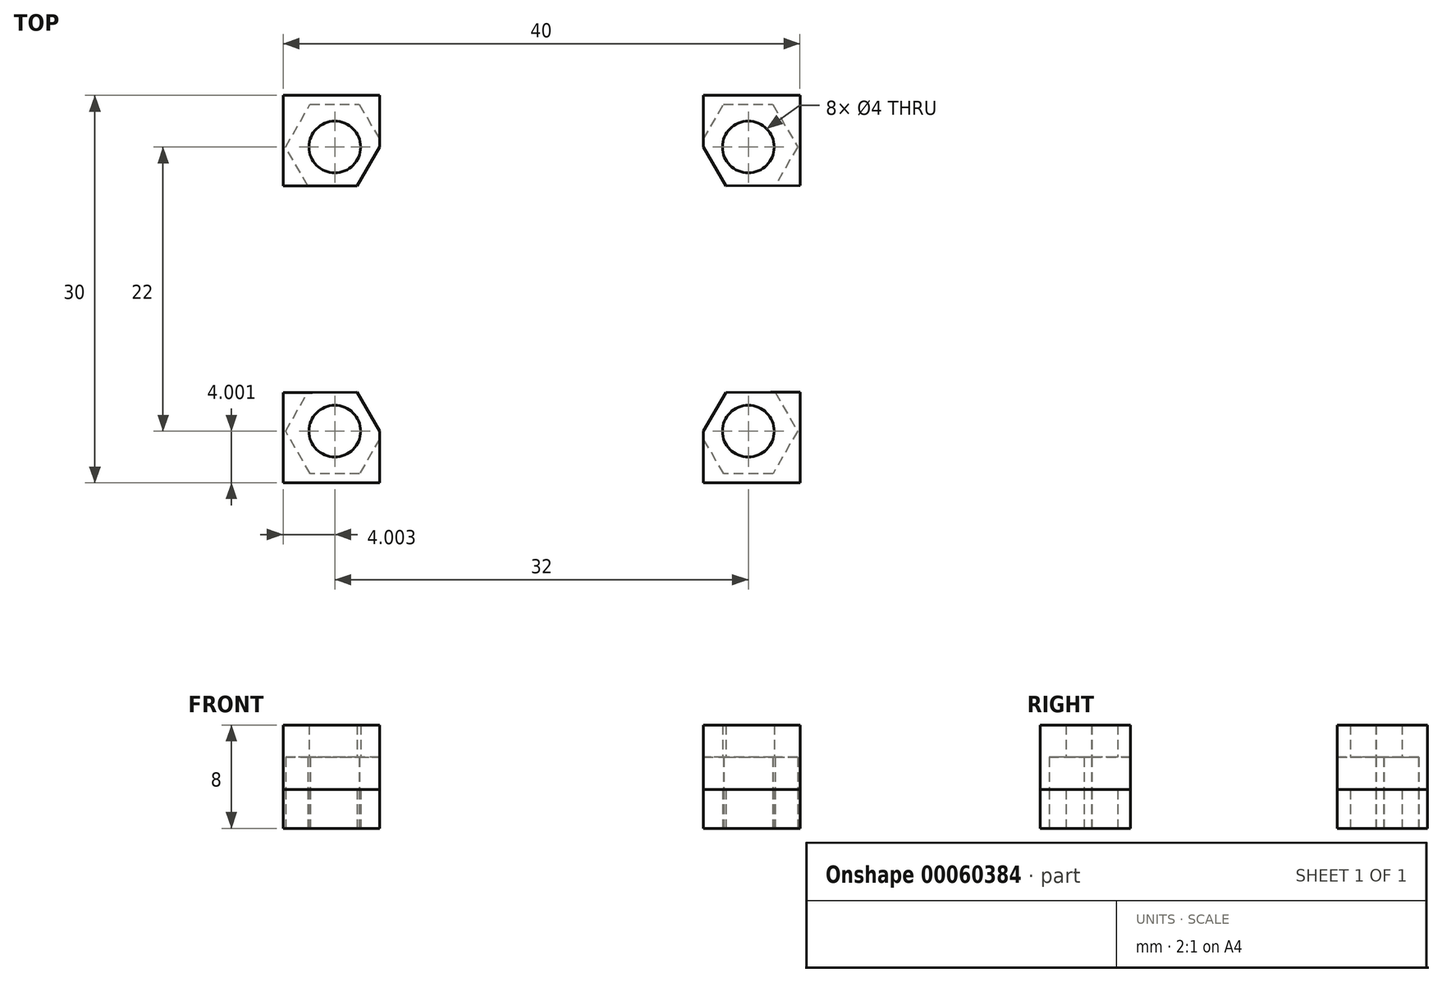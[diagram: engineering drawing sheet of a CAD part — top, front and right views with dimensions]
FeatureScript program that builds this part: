
annotation { "Feature Type Name" : "Feature", "Feature Type Description" : "" }
export const myFeature = defineFeature(function(context is Context, id is Id, definition is map)
    precondition{}
    {
        {
            var Q0;
            Q0=qCreatedBy(makeId("Top.planeOp"),FACE);
            var sketch = newSketch(context, id + "F0", { "sketchPlane" : qUnion([Q0])});
            skCircle(sketch, "E0.cCircle", {"center": v(0, 0) * mm, "radius": 3 * mm, "construction": true});
            skLineSegment(sketch, "E0.0", {"start": v(1.73, 3) * mm, "end": v(3.46, 0) * mm});
            skLineSegment(sketch, "E0.1", {"start": v(3.46, 0) * mm, "end": v(1.74, -3) * mm});
            skLineSegment(sketch, "E0.2", {"start": v(1.74, -3) * mm, "end": v(-1.73, -3) * mm});
            skLineSegment(sketch, "E0.3", {"start": v(-1.73, -3) * mm, "end": v(-3.46, 0) * mm});
            skLineSegment(sketch, "E0.4", {"start": v(-3.46, 0) * mm, "end": v(-1.74, 3) * mm});
            skLineSegment(sketch, "E0.5", {"start": v(-1.74, 3) * mm, "end": v(1.73, 3) * mm});
            skPoint(sketch, "E0.0.midPoint", {"position": v(2.6, 1.5) * mm});
            skCircle(sketch, "E1", {"center": v(0, 0) * mm, "radius": 1.5 * mm});
            skLineSegment(sketch, "E2.bottom", {"start": v(16.24, 59.41) * mm, "end": v(56.24, 59.41) * mm});
            skLineSegment(sketch, "E2.top", {"start": v(16.24, 29.41) * mm, "end": v(56.24, 29.41) * mm});
            skLineSegment(sketch, "E2.left", {"start": v(16.24, 59.41) * mm, "end": v(16.24, 29.41) * mm});
            skLineSegment(sketch, "E2.right", {"start": v(56.24, 59.41) * mm, "end": v(56.24, 29.41) * mm});
            skPoint(sketch, "E3.0.midPoint", {"position": v(22.84, 56.92) * mm});
            skLineSegment(sketch, "E3.3", {"start": v(18.52, 52.4) * mm, "end": v(16.78, 55.4) * mm, "construction": true});
            skLineSegment(sketch, "E3.2", {"start": v(21.98, 52.41) * mm, "end": v(18.52, 52.4) * mm});
            skLineSegment(sketch, "E3.1", {"start": v(23.7, 55.42) * mm, "end": v(21.98, 52.41) * mm});
            skLineSegment(sketch, "E3.0", {"start": v(21.97, 58.41) * mm, "end": v(23.7, 55.42) * mm, "construction": true});
            skLineSegment(sketch, "E3.4", {"start": v(16.78, 55.4) * mm, "end": v(18.5, 58.4) * mm, "construction": true});
            skLineSegment(sketch, "E3.5", {"start": v(18.5, 58.4) * mm, "end": v(21.97, 58.41) * mm, "construction": true});
            skCircle(sketch, "E4", {"center": v(20.24, 55.41) * mm, "radius": 1.5 * mm, "construction": true});
            skCircle(sketch, "E3.cCircle", {"center": v(20.24, 55.41) * mm, "radius": 3 * mm, "construction": true});
            skPoint(sketch, "E5.0.midPoint", {"position": v(22.84, 34.92) * mm});
            skLineSegment(sketch, "E5.3", {"start": v(18.52, 30.4) * mm, "end": v(16.78, 33.4) * mm, "construction": true});
            skLineSegment(sketch, "E5.2", {"start": v(21.98, 30.41) * mm, "end": v(18.52, 30.4) * mm, "construction": true});
            skLineSegment(sketch, "E5.1", {"start": v(23.7, 33.42) * mm, "end": v(21.98, 30.41) * mm, "construction": true});
            skLineSegment(sketch, "E5.0", {"start": v(21.97, 36.41) * mm, "end": v(23.7, 33.42) * mm});
            skLineSegment(sketch, "E5.4", {"start": v(16.78, 33.4) * mm, "end": v(18.5, 36.4) * mm, "construction": true});
            skLineSegment(sketch, "E5.5", {"start": v(18.5, 36.4) * mm, "end": v(21.97, 36.41) * mm});
            skCircle(sketch, "E6", {"center": v(20.24, 33.41) * mm, "radius": 1.5 * mm, "construction": true});
            skCircle(sketch, "E5.cCircle", {"center": v(20.24, 33.41) * mm, "radius": 3 * mm, "construction": true});
            skPoint(sketch, "E7.0.midPoint", {"position": v(54.84, 56.92) * mm});
            skLineSegment(sketch, "E7.3", {"start": v(50.52, 52.4) * mm, "end": v(48.78, 55.4) * mm});
            skLineSegment(sketch, "E7.2", {"start": v(53.98, 52.41) * mm, "end": v(50.52, 52.4) * mm});
            skLineSegment(sketch, "E7.1", {"start": v(55.7, 55.42) * mm, "end": v(53.98, 52.41) * mm, "construction": true});
            skLineSegment(sketch, "E7.0", {"start": v(53.97, 58.41) * mm, "end": v(55.7, 55.42) * mm, "construction": true});
            skLineSegment(sketch, "E7.4", {"start": v(48.78, 55.4) * mm, "end": v(50.5, 58.4) * mm, "construction": true});
            skLineSegment(sketch, "E7.5", {"start": v(50.5, 58.4) * mm, "end": v(53.97, 58.41) * mm, "construction": true});
            skCircle(sketch, "E8", {"center": v(52.24, 55.41) * mm, "radius": 1.5 * mm, "construction": true});
            skCircle(sketch, "E7.cCircle", {"center": v(52.24, 55.41) * mm, "radius": 3 * mm, "construction": true});
            skPoint(sketch, "E9.0.midPoint", {"position": v(54.84, 34.92) * mm});
            skLineSegment(sketch, "E9.3", {"start": v(50.52, 30.4) * mm, "end": v(48.78, 33.4) * mm, "construction": true});
            skLineSegment(sketch, "E9.2", {"start": v(53.98, 30.41) * mm, "end": v(50.52, 30.4) * mm, "construction": true});
            skLineSegment(sketch, "E9.1", {"start": v(55.7, 33.42) * mm, "end": v(53.98, 30.41) * mm, "construction": true});
            skLineSegment(sketch, "E9.0", {"start": v(53.97, 36.41) * mm, "end": v(55.7, 33.42) * mm, "construction": true});
            skLineSegment(sketch, "E9.4", {"start": v(48.78, 33.4) * mm, "end": v(50.5, 36.4) * mm});
            skLineSegment(sketch, "E9.5", {"start": v(50.5, 36.4) * mm, "end": v(53.97, 36.41) * mm});
            skCircle(sketch, "E10", {"center": v(52.24, 33.41) * mm, "radius": 1.5 * mm, "construction": true});
            skCircle(sketch, "E9.cCircle", {"center": v(52.24, 33.41) * mm, "radius": 3 * mm, "construction": true});
            skLineSegment(sketch, "E11", {"start": v(48.78, 33.4) * mm, "end": v(48.78, 29.41) * mm});
            skLineSegment(sketch, "E12", {"start": v(53.97, 36.41) * mm, "end": v(56.24, 36.41) * mm});
            skCircle(sketch, "E13.0", {"center": v(52.24, 33.41) * mm, "radius": 2 * mm});
            skLineSegment(sketch, "E14.0", {"start": v(50.34, 30.1) * mm, "end": v(48.52, 33.25) * mm});
            skLineSegment(sketch, "E14.1", {"start": v(54.15, 30.11) * mm, "end": v(50.34, 30.1) * mm});
            skLineSegment(sketch, "E14.2", {"start": v(56.05, 33.42) * mm, "end": v(54.15, 30.11) * mm});
            skLineSegment(sketch, "E14.3", {"start": v(54.23, 36.56) * mm, "end": v(56.05, 33.42) * mm});
            skLineSegment(sketch, "E15", {"start": v(23.7, 33.42) * mm, "end": v(23.7, 29.41) * mm});
            skLineSegment(sketch, "E16", {"start": v(18.5, 36.4) * mm, "end": v(16.24, 36.4) * mm});
            skLineSegment(sketch, "E17", {"start": v(18.52, 52.4) * mm, "end": v(16.24, 52.4) * mm});
            skLineSegment(sketch, "E18", {"start": v(23.7, 55.42) * mm, "end": v(23.7, 59.41) * mm});
            skLineSegment(sketch, "E19", {"start": v(53.98, 52.41) * mm, "end": v(56.24, 52.42) * mm});
            skLineSegment(sketch, "E20", {"start": v(48.78, 55.4) * mm, "end": v(48.78, 59.41) * mm});
            skCircle(sketch, "E21.0", {"center": v(52.24, 55.41) * mm, "radius": 2 * mm});
            skCircle(sketch, "E22.0", {"center": v(20.24, 55.41) * mm, "radius": 2 * mm});
            skCircle(sketch, "E23.0", {"center": v(20.24, 33.41) * mm, "radius": 2 * mm});
            skLineSegment(sketch, "E24.0", {"start": v(22.14, 58.71) * mm, "end": v(23.97, 55.57) * mm});
            skLineSegment(sketch, "E24.1", {"start": v(18.33, 58.7) * mm, "end": v(22.14, 58.71) * mm});
            skLineSegment(sketch, "E24.2", {"start": v(16.43, 55.4) * mm, "end": v(18.33, 58.7) * mm});
            skLineSegment(sketch, "E24.3", {"start": v(18.26, 52.26) * mm, "end": v(16.43, 55.4) * mm});
            skLineSegment(sketch, "E25.0", {"start": v(16.43, 33.4) * mm, "end": v(18.24, 36.56) * mm});
            skLineSegment(sketch, "E25.1", {"start": v(18.34, 30.1) * mm, "end": v(16.43, 33.4) * mm});
            skLineSegment(sketch, "E25.2", {"start": v(22.15, 30.11) * mm, "end": v(18.34, 30.1) * mm});
            skLineSegment(sketch, "E25.3", {"start": v(23.97, 33.27) * mm, "end": v(22.15, 30.11) * mm});
            skLineSegment(sketch, "E26.0", {"start": v(56.05, 55.42) * mm, "end": v(54.24, 52.26) * mm});
            skLineSegment(sketch, "E26.1", {"start": v(54.14, 58.71) * mm, "end": v(56.05, 55.42) * mm});
            skLineSegment(sketch, "E26.2", {"start": v(50.33, 58.7) * mm, "end": v(54.14, 58.71) * mm});
            skLineSegment(sketch, "E26.3", {"start": v(48.52, 55.55) * mm, "end": v(50.33, 58.7) * mm});
            skSolve(sketch);
        }
        {
            var Q0;
            {var subQ12=sQuery(id+"F0.wireOp",EDGE,"E14.1");Q0=makeQuery(id+"F0.imprint","IMPRINT",FACE,{"disambiguationData":[TD([[makeQuery(id+"F0.imprint","IMPRINT",EDGE,{"derivedFrom":subQ12}),1.0]])]});}
            var Q1;
            {var subQ6=sQuery(id+"F0.wireOp",EDGE,"E9.4");Q1=makeQuery(id+"F0.imprint","IMPRINT",FACE,{"disambiguationData":[TD([[makeQuery(id+"F0.imprint","IMPRINT",EDGE,{"derivedFrom":subQ6}),-1.0]])]});}
            var Q2;
            {var subQ5=sQuery(id+"F0.wireOp",EDGE,"E25.1");Q2=makeQuery(id+"F0.imprint","IMPRINT",FACE,{"disambiguationData":[TD([[makeQuery(id+"F0.imprint","IMPRINT",EDGE,{"derivedFrom":subQ5}),1.0]])]});}
            var Q3;
            {var subQ5=sQuery(id+"F0.wireOp",EDGE,"E5.0");Q3=makeQuery(id+"F0.imprint","IMPRINT",FACE,{"disambiguationData":[TD([[makeQuery(id+"F0.imprint","IMPRINT",EDGE,{"derivedFrom":subQ5}),-1.0]])]});}
            var Q4;
            {var subQ11=sQuery(id+"F0.wireOp",EDGE,"E24.1");Q4=makeQuery(id+"F0.imprint","IMPRINT",FACE,{"disambiguationData":[TD([[makeQuery(id+"F0.imprint","IMPRINT",EDGE,{"derivedFrom":subQ11}),1.0]])]});}
            var Q5;
            {var subQ5=sQuery(id+"F0.wireOp",EDGE,"E3.2");Q5=makeQuery(id+"F0.imprint","IMPRINT",FACE,{"disambiguationData":[TD([[makeQuery(id+"F0.imprint","IMPRINT",EDGE,{"derivedFrom":subQ5}),-1.0]])]});}
            var Q6;
            {var subQ7=sQuery(id+"F0.wireOp",EDGE,"E26.1");Q6=makeQuery(id+"F0.imprint","IMPRINT",FACE,{"disambiguationData":[TD([[makeQuery(id+"F0.imprint","IMPRINT",EDGE,{"derivedFrom":subQ7}),1.0]])]});}
            var Q7;
            {var subQ1=sQuery(id+"F0.wireOp",EDGE,"E7.3");Q7=makeQuery(id+"F0.imprint","IMPRINT",FACE,{"disambiguationData":[TD([[makeQuery(id+"F0.imprint","IMPRINT",EDGE,{"derivedFrom":subQ1}),-1.0]])]});}
            extrude(context, id + "F1", {"entities" : qUnion([Q0, Q1, Q2, Q3, Q4, Q5, Q6, Q7]), "depth" : 3 * mm});
        }
        {
            var Q0;
            {var subQ12=sQuery(id+"F0.wireOp",EDGE,"E14.1");Q0=makeQuery(id+"F0.imprint","IMPRINT",FACE,{"disambiguationData":[TD([[makeQuery(id+"F0.imprint","IMPRINT",EDGE,{"derivedFrom":subQ12}),1.0]])]});}
            var Q1;
            {var subQ7=sQuery(id+"F0.wireOp",EDGE,"E26.1");Q1=makeQuery(id+"F0.imprint","IMPRINT",FACE,{"disambiguationData":[TD([[makeQuery(id+"F0.imprint","IMPRINT",EDGE,{"derivedFrom":subQ7}),1.0]])]});}
            var Q2;
            {var subQ11=sQuery(id+"F0.wireOp",EDGE,"E24.1");Q2=makeQuery(id+"F0.imprint","IMPRINT",FACE,{"disambiguationData":[TD([[makeQuery(id+"F0.imprint","IMPRINT",EDGE,{"derivedFrom":subQ11}),1.0]])]});}
            var Q3;
            {var subQ5=sQuery(id+"F0.wireOp",EDGE,"E25.1");Q3=makeQuery(id+"F0.imprint","IMPRINT",FACE,{"disambiguationData":[TD([[makeQuery(id+"F0.imprint","IMPRINT",EDGE,{"derivedFrom":subQ5}),1.0]])]});}
            extrude(context, id + "F2", {"entities" : qUnion([Q0, Q1, Q2, Q3]), "endBound" : BoundingType.UP_TO_NEXT, "depth" : 25 * mm});
        }
        {
            var Q0;
            Q0=makeQuery(id+"F2.opExtrude","CAP_FACE",FACE,{"disambiguationData":[OSD([sQuery(id+"F0.wireOp",EDGE,"E2.top"),sQuery(id+"F0.wireOp",EDGE,"E2.right"),sQuery(id+"F0.wireOp",EDGE,"E9.4"),sQuery(id+"F0.wireOp",EDGE,"E9.5"),sQuery(id+"F0.wireOp",EDGE,"E11"),sQuery(id+"F0.wireOp",EDGE,"E12"),sQuery(id+"F0.wireOp",EDGE,"E13.0")])],"isStart":false});
            var Q1;
            Q1=makeQuery(id+"F2.opExtrude","CAP_FACE",FACE,{"disambiguationData":[OSD([sQuery(id+"F0.wireOp",EDGE,"E2.top"),sQuery(id+"F0.wireOp",EDGE,"E2.left"),sQuery(id+"F0.wireOp",EDGE,"E5.0"),sQuery(id+"F0.wireOp",EDGE,"E5.5"),sQuery(id+"F0.wireOp",EDGE,"E15"),sQuery(id+"F0.wireOp",EDGE,"E16"),sQuery(id+"F0.wireOp",EDGE,"E23.0")])],"isStart":false});
            var Q2;
            Q2=makeQuery(id+"F2.opExtrude","CAP_FACE",FACE,{"disambiguationData":[OSD([sQuery(id+"F0.wireOp",EDGE,"E2.bottom"),sQuery(id+"F0.wireOp",EDGE,"E2.left"),sQuery(id+"F0.wireOp",EDGE,"E3.2"),sQuery(id+"F0.wireOp",EDGE,"E3.1"),sQuery(id+"F0.wireOp",EDGE,"E17"),sQuery(id+"F0.wireOp",EDGE,"E18"),sQuery(id+"F0.wireOp",EDGE,"E22.0")])],"isStart":false});
            var Q3;
            Q3=makeQuery(id+"F2.opExtrude","CAP_FACE",FACE,{"disambiguationData":[OSD([sQuery(id+"F0.wireOp",EDGE,"E2.bottom"),sQuery(id+"F0.wireOp",EDGE,"E2.right"),sQuery(id+"F0.wireOp",EDGE,"E7.3"),sQuery(id+"F0.wireOp",EDGE,"E7.2"),sQuery(id+"F0.wireOp",EDGE,"E19"),sQuery(id+"F0.wireOp",EDGE,"E20"),sQuery(id+"F0.wireOp",EDGE,"E21.0")])],"isStart":false});
            extrude(context, id + "F3", {"entities" : qUnion([Q0, Q1, Q2, Q3]), "depth" : 2.5 * mm});
        }
        {
            var Q0;
            Q0=makeQuery(id+"F1.opExtrude","CAP_FACE",FACE,{"disambiguationData":[OSD([sQuery(id+"F0.wireOp",EDGE,"E2.top"),sQuery(id+"F0.wireOp",EDGE,"E2.right"),sQuery(id+"F0.wireOp",EDGE,"E9.4"),sQuery(id+"F0.wireOp",EDGE,"E9.5"),sQuery(id+"F0.wireOp",EDGE,"E11"),sQuery(id+"F0.wireOp",EDGE,"E12"),sQuery(id+"F0.wireOp",EDGE,"E13.0")])],"isStart":false});
            var Q1;
            Q1=makeQuery(id+"F1.opExtrude","CAP_FACE",FACE,{"disambiguationData":[OSD([sQuery(id+"F0.wireOp",EDGE,"E2.top"),sQuery(id+"F0.wireOp",EDGE,"E2.left"),sQuery(id+"F0.wireOp",EDGE,"E5.0"),sQuery(id+"F0.wireOp",EDGE,"E5.5"),sQuery(id+"F0.wireOp",EDGE,"E15"),sQuery(id+"F0.wireOp",EDGE,"E16"),sQuery(id+"F0.wireOp",EDGE,"E23.0")])],"isStart":false});
            var Q2;
            Q2=makeQuery(id+"F1.opExtrude","CAP_FACE",FACE,{"disambiguationData":[OSD([sQuery(id+"F0.wireOp",EDGE,"E2.bottom"),sQuery(id+"F0.wireOp",EDGE,"E2.left"),sQuery(id+"F0.wireOp",EDGE,"E3.2"),sQuery(id+"F0.wireOp",EDGE,"E3.1"),sQuery(id+"F0.wireOp",EDGE,"E17"),sQuery(id+"F0.wireOp",EDGE,"E18"),sQuery(id+"F0.wireOp",EDGE,"E22.0")])],"isStart":false});
            var Q3;
            Q3=makeQuery(id+"F1.opExtrude","CAP_FACE",FACE,{"disambiguationData":[OSD([sQuery(id+"F0.wireOp",EDGE,"E2.bottom"),sQuery(id+"F0.wireOp",EDGE,"E2.right"),sQuery(id+"F0.wireOp",EDGE,"E7.3"),sQuery(id+"F0.wireOp",EDGE,"E7.2"),sQuery(id+"F0.wireOp",EDGE,"E19"),sQuery(id+"F0.wireOp",EDGE,"E20"),sQuery(id+"F0.wireOp",EDGE,"E21.0")])],"isStart":false});
            extrude(context, id + "F4", {"entities" : qUnion([Q0, Q1, Q2, Q3]), "operationType" : NewBodyOperationType.ADD, "depth" : 5 * mm, "hasSecondDirection" : true, "secondDirectionOppositeDirection" : false, "secondDirectionDepth" : 2.5 * mm});
        }
    });
